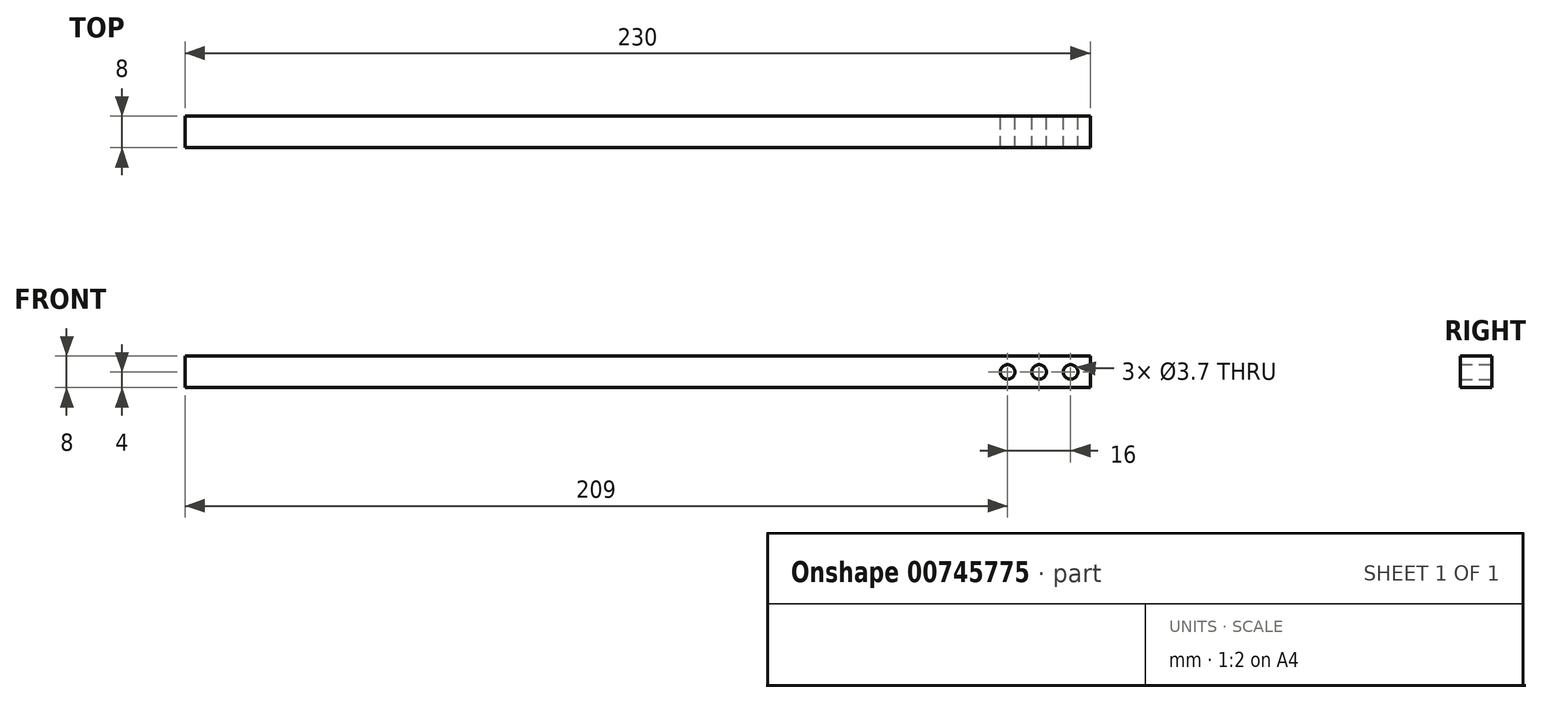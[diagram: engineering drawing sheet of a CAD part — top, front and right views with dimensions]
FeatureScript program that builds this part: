
annotation { "Feature Type Name" : "Feature", "Feature Type Description" : "" }
export const myFeature = defineFeature(function(context is Context, id is Id, definition is map)
    precondition{}
    {
        {
            var Q0;
            Q0=qCreatedBy(makeId("Front.planeOp"),FACE);
            var sketch = newSketch(context, id + "F0", { "sketchPlane" : qUnion([Q0])});
            skLineSegment(sketch, "E0.bottom", {"start": v(0, 0) * mm, "end": v(-230, 0) * mm});
            skLineSegment(sketch, "E0.top", {"start": v(0, 8) * mm, "end": v(-230, 8) * mm});
            skLineSegment(sketch, "E0.left", {"start": v(0, 0) * mm, "end": v(0, 8) * mm});
            skLineSegment(sketch, "E0.right", {"start": v(-230, 0) * mm, "end": v(-230, 8) * mm});
            skCircle(sketch, "E1", {"center": v(-5, 4) * mm, "radius": 1.85 * mm});
            skPoint(sketch, "E1.centerSnap0", {"position": v(0, 4) * mm});
            skCircle(sketch, "E2", {"center": v(-21, 4) * mm, "radius": 1.85 * mm});
            skCircle(sketch, "E3", {"center": v(-13, 4) * mm, "radius": 1.85 * mm});
            skSolve(sketch);
        }
        {
            var Q0;
            Q0=makeQuery(id+"F0.imprint","IMPRINT",FACE,{"disambiguationData":[TD([[makeQuery(id+"F0.imprint","IMPRINT",EDGE,{"derivedFrom":sQuery(id+"F0.wireOp",EDGE,"E0.bottom")}),-1.0]])]});
            extrude(context, id + "F1", {"entities" : qUnion([Q0]), "depth" : 8 * mm, "offsetDistance" : 25 * mm});
        }
    });
